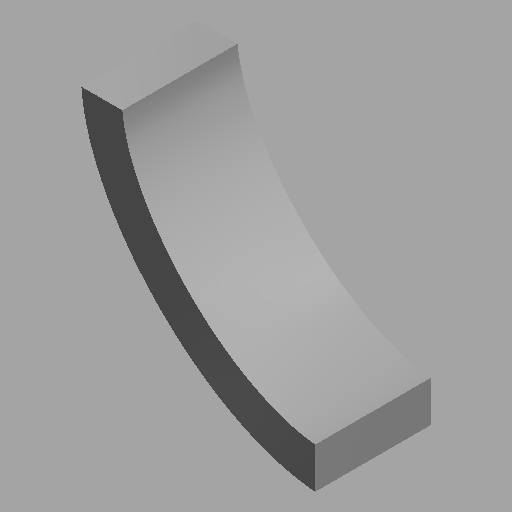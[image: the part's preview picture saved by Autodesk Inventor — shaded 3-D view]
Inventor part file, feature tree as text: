
AUTODESK INVENTOR PART (.ipt)
format: ipt  version: 2023 (Build 270158030, 158C)  size: 114,688 bytes
history: native  units: mm (DEFAULTED — no unit token found)
features: direct_edit x2, other x1, revolve x1, move_body x1
ambient origin geometry x8: Origin, YZ Plane, XZ Plane, XY Plane, X Axis, Y Axis, Z Axis, Center Point
bodies: Solid1 (feature_tree)
feature tree (5):
  other  "Arch header 2 (C)"
  direct_edit  "Direct Edit1"
  direct_edit  "Direct Edit2"
  revolve  "Rotate1"  Angle=135.0deg
  move_body  "Move1"
